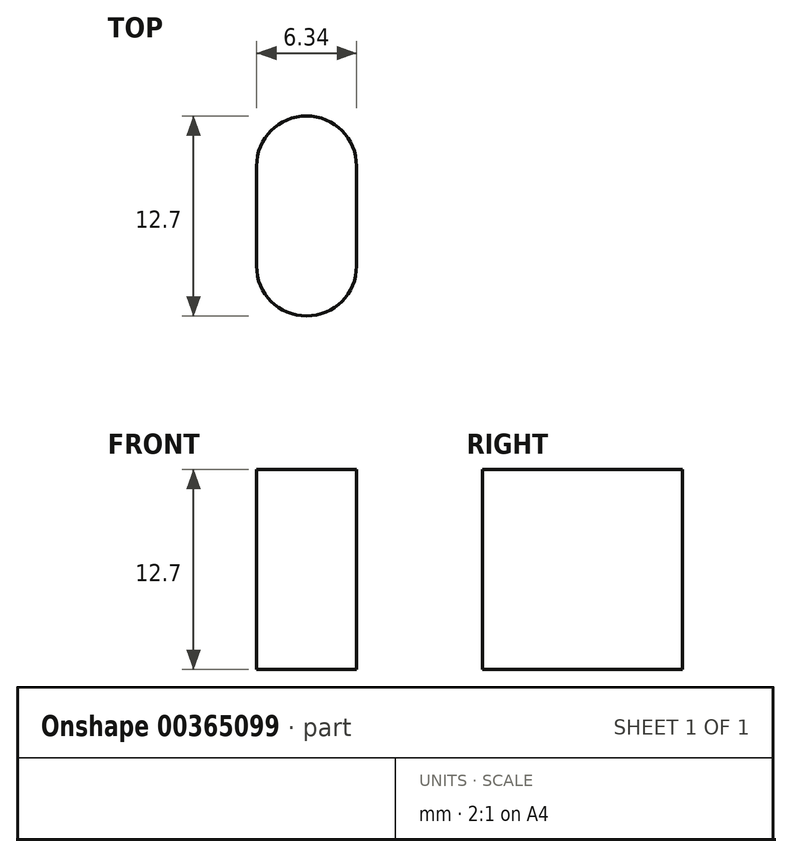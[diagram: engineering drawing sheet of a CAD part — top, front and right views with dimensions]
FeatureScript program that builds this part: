
annotation { "Feature Type Name" : "Feature", "Feature Type Description" : "" }
export const myFeature = defineFeature(function(context is Context, id is Id, definition is map)
    precondition{}
    {
        {
            var Q0;
            Q0=qCreatedBy(makeId("Top.planeOp"),FACE);
            var sketch = newSketch(context, id + "F0", { "sketchPlane" : qUnion([Q0])});
            skLineSegment(sketch, "E0", {"start": v(0, -3.18) * mm, "end": v(0, 3.18) * mm});
            skArc(sketch, "E1.0.startCap", {"start": v(3.18, -3.18) * mm, "mid": v(0, -6.35) * mm, "end": v(-3.18, -3.18) * mm});
            skArc(sketch, "E1.0.endCap", {"start": v(-3.18, 3.18) * mm, "mid": v(0, 6.35) * mm, "end": v(3.17, 3.18) * mm});
            skLineSegment(sketch, "E1.0.left", {"start": v(-3.18, -3.18) * mm, "end": v(-3.18, 3.17) * mm});
            skLineSegment(sketch, "E1.0.right", {"start": v(3.17, -3.18) * mm, "end": v(3.17, 3.18) * mm});
            skLineSegment(sketch, "E2.bottom", {"start": v(14.3, -17.7) * mm, "end": v(-14.3, -17.7) * mm});
            skLineSegment(sketch, "E2.top", {"start": v(14.3, 17.7) * mm, "end": v(-14.3, 17.7) * mm});
            skLineSegment(sketch, "E2.left", {"start": v(14.3, -17.7) * mm, "end": v(14.3, 17.7) * mm});
            skLineSegment(sketch, "E2.right", {"start": v(-14.3, -17.7) * mm, "end": v(-14.3, 17.7) * mm});
            skPoint(sketch, "E2.middle", {"position": v(0, 0) * mm});
            skSolve(sketch);
        }
        {
            var Q0;
            Q0=makeQuery(id+"F0.imprint","IMPRINT",FACE,{"disambiguationData":[TD([[makeQuery(id+"F0.imprint","IMPRINT",EDGE,{"derivedFrom":sQuery(id+"F0.wireOp",EDGE,"E1.0.startCap")}),1.0]])]});
            extrude(context, id + "F1", {"entities" : qUnion([Q0]), "depth" : 12.7 * mm});
        }
    });
